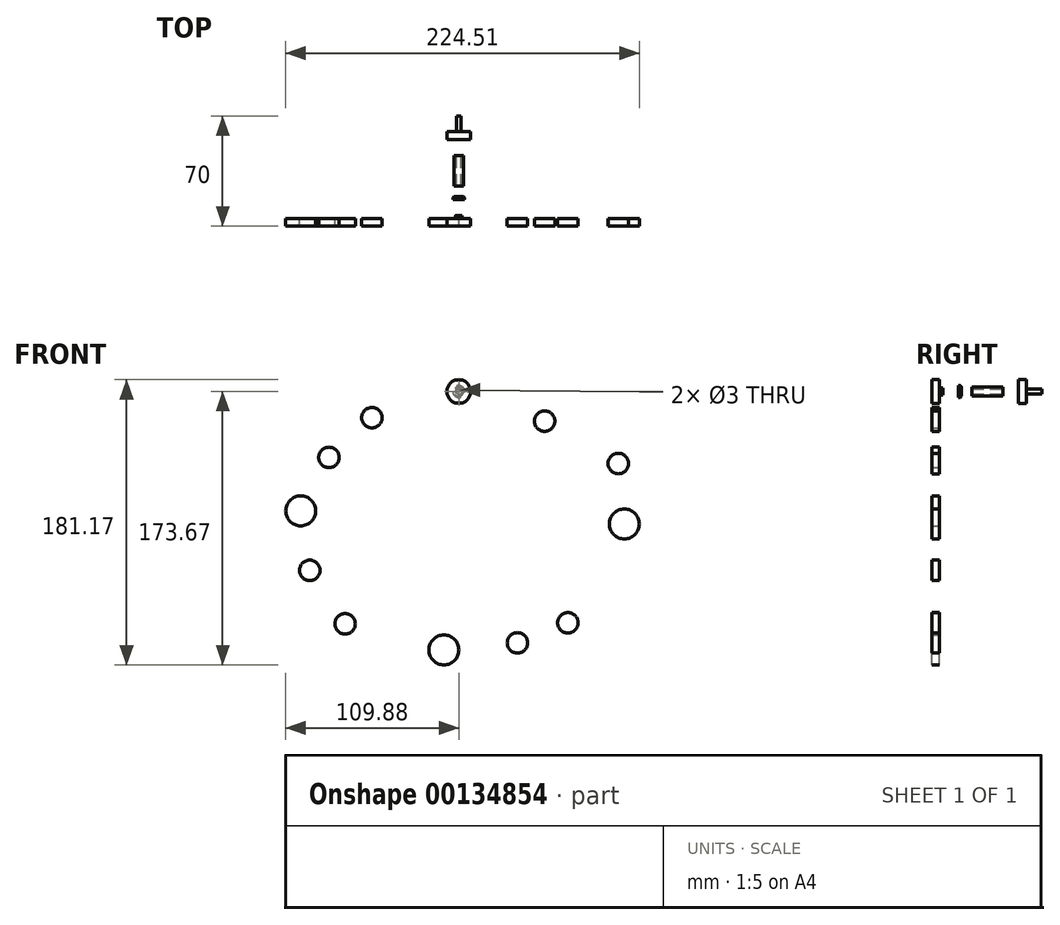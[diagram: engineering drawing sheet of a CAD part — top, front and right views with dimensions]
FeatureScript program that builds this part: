
annotation { "Feature Type Name" : "Feature", "Feature Type Description" : "" }
export const myFeature = defineFeature(function(context is Context, id is Id, definition is map)
    precondition{}
    {
        {
            var Q0;
            Q0=qCreatedBy(makeId("Front.planeOp"),FACE);
            var sketch = newSketch(context, id + "F0", { "sketchPlane" : qUnion([Q0])});
            skCircle(sketch, "E0", {"center": v(0, 0) * mm, "radius": 7.5 * mm});
            skSolve(sketch);
        }
        {
            var Q0;
            Q0=qSketchRegion(id+"F0",true);
            extrude(context, id + "F1", {"entities" : qUnion([Q0]), "depth" : 5 * mm});
        }
        {
            var Q0;
            Q0=makeQuery(id+"F1.opExtrude","CAP_FACE",FACE,{"disambiguationData":[OSD([sQuery(id+"F0.wireOp",EDGE,"E0")])],"isStart":true});
            var sketch = newSketch(context, id + "F2", { "sketchPlane" : qUnion([Q0])});
            skCircle(sketch, "E1", {"center": v(0, 0) * mm, "radius": 2.25 * mm});
            skSolve(sketch);
        }
        {
            var Q0;
            Q0=qSketchRegion(id+"F2",true);
            extrude(context, id + "F3", {"entities" : qUnion([Q0]), "operationType" : NewBodyOperationType.ADD, "depth" : 1.9 * mm, "hasDraft" : true, "draftAngle" : 5 * degree, "draftPullDirection" : true});
        }
        {
            var Q0;
            Q0=makeQuery(id+"F3.opExtrude","CAP_FACE",FACE,{"disambiguationData":[OSD([sQuery(id+"F2.wireOp",EDGE,"E1")])],"isStart":false});
            var sketch = newSketch(context, id + "F4", { "sketchPlane" : qUnion([Q0])});
            skCircle(sketch, "E2", {"center": v(0, 0) * mm, "radius": 1.5 * mm});
            skSolve(sketch);
        }
        {
            var Q0;
            Q0=makeQuery(id+"F3.opExtrude","CAP_FACE",FACE,{"disambiguationData":[OSD([sQuery(id+"F2.wireOp",EDGE,"E1")])],"isStart":false});
            cPlane(context, id + "F5", {"entities" : qUnion([Q0]), "cplaneType" : CPlaneType.OFFSET, "offset" : 10 * mm, "width" : 150 * mm, "height" : 150 * mm});
        }
        {
            var Q0;
            Q0=qCreatedBy(makeId("Front.planeOp"),FACE);
            cPlane(context, id + "F6", {"entities" : qUnion([Q0]), "cplaneType" : CPlaneType.OFFSET, "offset" : 40 * mm, "oppositeDirection" : true, "width" : 150 * mm, "height" : 150 * mm});
        }
        {
            var Q0;
            Q0=qCreatedBy(id+"F5.planeOp",FACE);
            var sketch = newSketch(context, id + "F7", { "sketchPlane" : qUnion([Q0])});
            skCircle(sketch, "E3", {"center": v(0, 0) * mm, "radius": 3.75 * mm});
            skSolve(sketch);
        }
        {
            var Q0;
            Q0=makeQuery(id+"F7.imprint","IMPRINT",FACE,{"disambiguationData":[TD([[makeQuery(id+"F7.imprint","IMPRINT",EDGE,{"derivedFrom":sQuery(id+"F7.wireOp",EDGE,"E3")}),1.0]])]});
            extrude(context, id + "F8", {"entities" : qUnion([Q0]), "operationType" : NewBodyOperationType.ADD, "depth" : 2 * mm});
        }
        {
            var Q0;
            Q0=makeQuery(id+"F8.opExtrude","CAP_FACE",FACE,{"disambiguationData":[OSD([sQuery(id+"F7.wireOp",EDGE,"E3")])],"isStart":false});
            var sketch = newSketch(context, id + "F9", { "sketchPlane" : qUnion([Q0])});
            skCircle(sketch, "E4.0.0", {"center": v(0, 0) * mm, "radius": 7.5 * mm});
            skCircle(sketch, "E5", {"center": v(0, 0) * mm, "radius": 1.5 * mm});
            skSolve(sketch);
        }
        {
            var Q0;
            Q0=makeQuery(id+"F9.imprint","IMPRINT",FACE,{"disambiguationData":[TD([[makeQuery(id+"F9.imprint","IMPRINT",EDGE,{"derivedFrom":sQuery(id+"F9.wireOp",EDGE,"E5")}),1.0]])]});
            extrude(context, id + "F10", {"entities" : qUnion([Q0]), "operationType" : NewBodyOperationType.REMOVE, "oppositeDirection" : true, "depth" : 2 * mm});
        }
        {
            var Q0;
            Q0=makeQuery(id+"F8.opExtrude","CAP_EDGE",EDGE,{"disambiguationData":[OSD([sQuery(id+"F7.wireOp",EDGE,"E3")])],"isStart":false});
            chamfer(context, id + "F11", {"entities" : qUnion([Q0]), "width" : .75 * mm, "tangentPropagation" : true});
        }
        {
            var Q0;
            Q0=qCreatedBy(id+"F6.planeOp",FACE);
            var sketch = newSketch(context, id + "F12", { "sketchPlane" : qUnion([Q0])});
            skCircle(sketch, "E6", {"center": v(0, 0) * mm, "radius": 3 * mm});
            skCircle(sketch, "E7.0", {"center": v(0, 0) * mm, "radius": 1.5 * mm, "construction": true});
            skCircle(sketch, "E8", {"center": v(0, 0) * mm, "radius": 1.5 * mm});
            skSolve(sketch);
        }
        {
            var Q0;
            Q0=makeQuery(id+"F12.imprint","IMPRINT",FACE,{"disambiguationData":[TD([[makeQuery(id+"F12.imprint","IMPRINT",EDGE,{"derivedFrom":sQuery(id+"F12.wireOp",EDGE,"E6")}),1.0]])]});
            extrude(context, id + "F13", {"entities" : qUnion([Q0]), "depth" : 19.5 * mm});
        }
        {
            var Q0;
            Q0=qCreatedBy(id+"F6.planeOp",FACE);
            cPlane(context, id + "F14", {"entities" : qUnion([Q0]), "cplaneType" : CPlaneType.OFFSET, "offset" : 10 * mm, "oppositeDirection" : true, "width" : 150 * mm, "height" : 150 * mm});
        }
        {
            var Q0;
            Q0=qCreatedBy(id+"F14.planeOp",FACE);
            var sketch = newSketch(context, id + "F15", { "sketchPlane" : qUnion([Q0])});
            skCircle(sketch, "E9.0.0", {"center": v(0, 0) * mm, "radius": 7.5 * mm});
            skCircle(sketch, "E10.0", {"center": v(0, 0) * mm, "radius": 3 * mm});
            skCircle(sketch, "E11.0", {"center": v(0, 0) * mm, "radius": 1.5 * mm});
            skSolve(sketch);
        }
        {
            var Q0;
            Q0=makeQuery(id+"F15.imprint","IMPRINT",FACE,{"disambiguationData":[TD([[makeQuery(id+"F15.imprint","IMPRINT",EDGE,{"derivedFrom":sQuery(id+"F15.wireOp",EDGE,"E9.0.0")}),1.0]])]});
            var Q1;
            Q1=makeQuery(id+"F15.imprint","IMPRINT",FACE,{"disambiguationData":[TD([[makeQuery(id+"F15.imprint","IMPRINT",EDGE,{"derivedFrom":sQuery(id+"F15.wireOp",EDGE,"E11.0")}),1.0]])]});
            var Q2;
            Q2=makeQuery(id+"F15.imprint","IMPRINT",FACE,{"disambiguationData":[TD([[makeQuery(id+"F15.imprint","IMPRINT",EDGE,{"derivedFrom":sQuery(id+"F15.wireOp",EDGE,"E10.0")}),1.0]])]});
            extrude(context, id + "F16", {"entities" : qUnion([Q0, Q1, Q2]), "oppositeDirection" : true, "depth" : 5 * mm});
        }
        {
            var Q0;
            Q0=makeQuery(id+"F15.imprint","IMPRINT",FACE,{"disambiguationData":[TD([[makeQuery(id+"F15.imprint","IMPRINT",EDGE,{"derivedFrom":sQuery(id+"F15.wireOp",EDGE,"E11.0")}),1.0]])]});
            extrude(context, id + "F17", {"entities" : qUnion([Q0]), "operationType" : NewBodyOperationType.ADD, "oppositeDirection" : true, "depth" : 15 * mm});
        }
        {
            var Q0;
            Q0=qCreatedBy(makeId("Front.planeOp"),FACE);
            var sketch = newSketch(context, id + "F18", { "sketchPlane" : qUnion([Q0])});
            skCircle(sketch, "E12", {"center": v(-55.22, -16.65) * mm, "radius": 6.5 * mm});
            skCircle(sketch, "E13", {"center": v(-82.46, -41.88) * mm, "radius": 6.5 * mm});
            skCircle(sketch, "E14", {"center": v(-100.38, -75.82) * mm, "radius": 9.5 * mm});
            skCircle(sketch, "E15", {"center": v(-94.62, -113.6) * mm, "radius": 6.5 * mm});
            skCircle(sketch, "E16", {"center": v(-72.21, -147.52) * mm, "radius": 6.5 * mm});
            skCircle(sketch, "E17", {"center": v(-9.47, -164.17) * mm, "radius": 9.5 * mm});
            skCircle(sketch, "E18", {"center": v(37.27, -159.69) * mm, "radius": 6.5 * mm});
            skCircle(sketch, "E19", {"center": v(69.28, -146.88) * mm, "radius": 6.5 * mm});
            skCircle(sketch, "E20", {"center": v(105.13, -84.14) * mm, "radius": 9.5 * mm});
            skCircle(sketch, "E21", {"center": v(101.3, -45.72) * mm, "radius": 6.5 * mm});
            skCircle(sketch, "E22", {"center": v(54.55, -18.83) * mm, "radius": 6.5 * mm});
            skSolve(sketch);
        }
        {
            var Q0;
            Q0=makeQuery(id+"F18.imprint","IMPRINT",FACE,{"disambiguationData":[TD([[makeQuery(id+"F18.imprint","IMPRINT",EDGE,{"derivedFrom":sQuery(id+"F18.wireOp",EDGE,"E12")}),1.0]])]});
            extrude(context, id + "F19", {"entities" : qUnion([Q0]), "depth" : 5 * mm});
        }
        {
            var Q0;
            Q0=makeQuery(id+"F18.imprint","IMPRINT",FACE,{"disambiguationData":[TD([[makeQuery(id+"F18.imprint","IMPRINT",EDGE,{"derivedFrom":sQuery(id+"F18.wireOp",EDGE,"E13")}),1.0]])]});
            extrude(context, id + "F20", {"entities" : qUnion([Q0]), "depth" : 5 * mm});
        }
        {
            var Q0;
            Q0=makeQuery(id+"F18.imprint","IMPRINT",FACE,{"disambiguationData":[TD([[makeQuery(id+"F18.imprint","IMPRINT",EDGE,{"derivedFrom":sQuery(id+"F18.wireOp",EDGE,"E14")}),1.0]])]});
            extrude(context, id + "F21", {"entities" : qUnion([Q0]), "depth" : 5 * mm});
        }
        {
            var Q0;
            Q0=makeQuery(id+"F18.imprint","IMPRINT",FACE,{"disambiguationData":[TD([[makeQuery(id+"F18.imprint","IMPRINT",EDGE,{"derivedFrom":sQuery(id+"F18.wireOp",EDGE,"E15")}),1.0]])]});
            extrude(context, id + "F22", {"entities" : qUnion([Q0]), "depth" : 5 * mm});
        }
        {
            var Q0;
            Q0=makeQuery(id+"F18.imprint","IMPRINT",FACE,{"disambiguationData":[TD([[makeQuery(id+"F18.imprint","IMPRINT",EDGE,{"derivedFrom":sQuery(id+"F18.wireOp",EDGE,"E16")}),1.0]])]});
            extrude(context, id + "F23", {"entities" : qUnion([Q0]), "depth" : 5 * mm});
        }
        {
            var Q0;
            Q0=makeQuery(id+"F18.imprint","IMPRINT",FACE,{"disambiguationData":[TD([[makeQuery(id+"F18.imprint","IMPRINT",EDGE,{"derivedFrom":sQuery(id+"F18.wireOp",EDGE,"E17")}),1.0]])]});
            extrude(context, id + "F24", {"entities" : qUnion([Q0]), "depth" : 5 * mm});
        }
        {
            var Q0;
            Q0=makeQuery(id+"F18.imprint","IMPRINT",FACE,{"disambiguationData":[TD([[makeQuery(id+"F18.imprint","IMPRINT",EDGE,{"derivedFrom":sQuery(id+"F18.wireOp",EDGE,"E18")}),1.0]])]});
            extrude(context, id + "F25", {"entities" : qUnion([Q0]), "depth" : 5 * mm});
        }
        {
            var Q0;
            Q0=makeQuery(id+"F18.imprint","IMPRINT",FACE,{"disambiguationData":[TD([[makeQuery(id+"F18.imprint","IMPRINT",EDGE,{"derivedFrom":sQuery(id+"F18.wireOp",EDGE,"E19")}),1.0]])]});
            extrude(context, id + "F26", {"entities" : qUnion([Q0]), "depth" : 5 * mm});
        }
        {
            var Q0;
            Q0=makeQuery(id+"F18.imprint","IMPRINT",FACE,{"disambiguationData":[TD([[makeQuery(id+"F18.imprint","IMPRINT",EDGE,{"derivedFrom":sQuery(id+"F18.wireOp",EDGE,"E20")}),1.0]])]});
            extrude(context, id + "F27", {"entities" : qUnion([Q0]), "depth" : 5 * mm});
        }
        {
            var Q0;
            Q0=makeQuery(id+"F18.imprint","IMPRINT",FACE,{"disambiguationData":[TD([[makeQuery(id+"F18.imprint","IMPRINT",EDGE,{"derivedFrom":sQuery(id+"F18.wireOp",EDGE,"E21")}),1.0]])]});
            extrude(context, id + "F28", {"entities" : qUnion([Q0]), "depth" : 5 * mm});
        }
        {
            var Q0;
            Q0=makeQuery(id+"F18.imprint","IMPRINT",FACE,{"disambiguationData":[TD([[makeQuery(id+"F18.imprint","IMPRINT",EDGE,{"derivedFrom":sQuery(id+"F18.wireOp",EDGE,"E22")}),1.0]])]});
            extrude(context, id + "F29", {"entities" : qUnion([Q0]), "depth" : 5 * mm});
        }
    });
